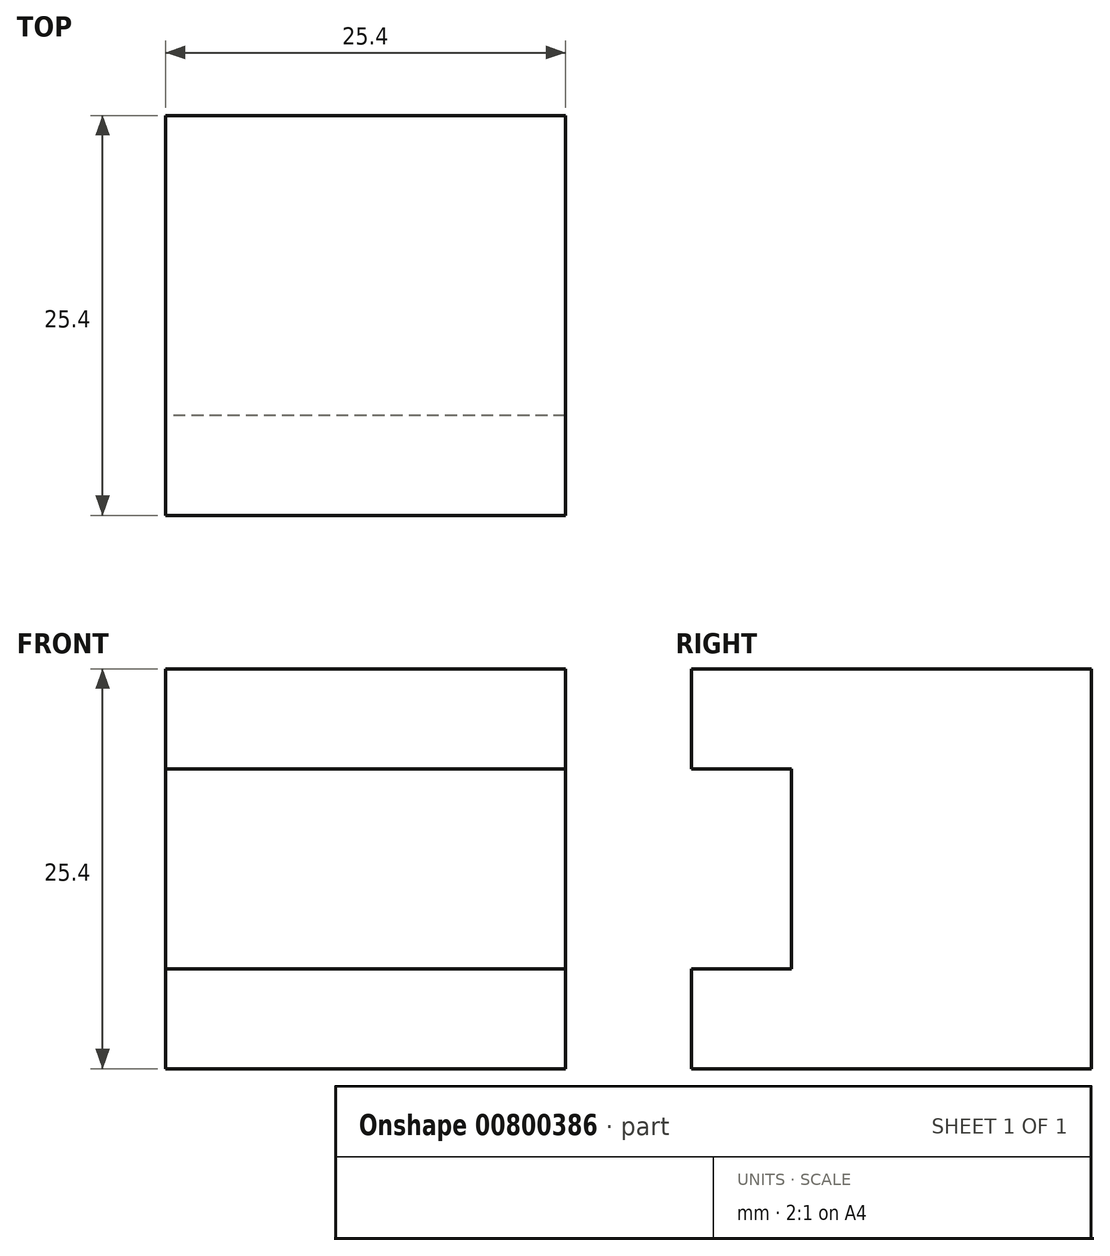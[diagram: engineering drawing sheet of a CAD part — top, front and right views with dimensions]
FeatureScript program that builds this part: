
annotation { "Feature Type Name" : "Feature", "Feature Type Description" : "" }
export const myFeature = defineFeature(function(context is Context, id is Id, definition is map)
    precondition{}
    {
        {
            var Q0;
            Q0=qCreatedBy(makeId("Right.planeOp"),FACE);
            var sketch = newSketch(context, id + "F0", { "sketchPlane" : qUnion([Q0])});
            skLineSegment(sketch, "E0", {"start": v(0, 0) * mm, "end": v(25.4, 0) * mm});
            skLineSegment(sketch, "E1", {"start": v(25.4, 0) * mm, "end": v(25.4, -25.4) * mm});
            skLineSegment(sketch, "E2", {"start": v(25.4, -25.4) * mm, "end": v(0, -25.4) * mm});
            skLineSegment(sketch, "E3", {"start": v(0, -25.4) * mm, "end": v(0, -19.05) * mm});
            skLineSegment(sketch, "E4", {"start": v(0, -19.05) * mm, "end": v(6.35, -19.05) * mm});
            skLineSegment(sketch, "E5", {"start": v(6.35, -19.05) * mm, "end": v(6.35, -6.35) * mm});
            skLineSegment(sketch, "E6", {"start": v(6.35, -6.35) * mm, "end": v(0, -6.35) * mm});
            skLineSegment(sketch, "E7", {"start": v(0, -6.35) * mm, "end": v(0, -2.7) * mm});
            skLineSegment(sketch, "E8", {"start": v(0, -2.7) * mm, "end": v(0, 0) * mm});
            skSolve(sketch);
        }
        {
            var Q0;
            Q0=makeQuery(id+"F0.imprint","IMPRINT",FACE,{"disambiguationData":[TD([[makeQuery(id+"F0.imprint","IMPRINT",EDGE,{"derivedFrom":sQuery(id+"F0.wireOp",EDGE,"E0")}),-1.0]])]});
            extrude(context, id + "F1", {"entities" : qUnion([Q0]), "depth" : 25.4 * mm, "offsetDistance" : 25.4 * mm});
        }
    });
